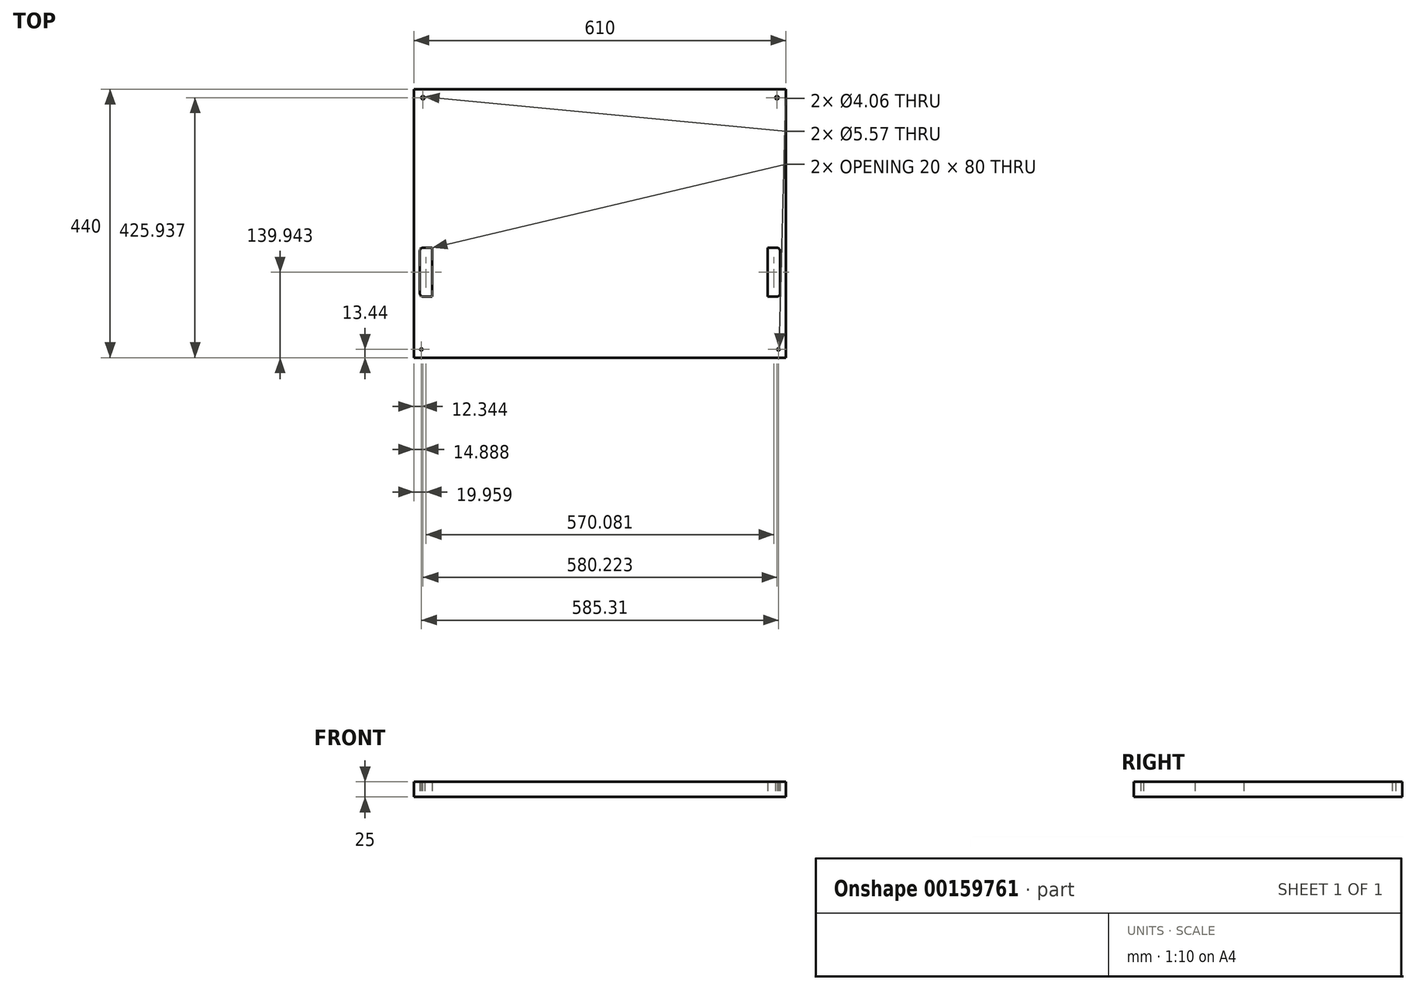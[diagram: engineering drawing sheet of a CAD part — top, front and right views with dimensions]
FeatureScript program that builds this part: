
annotation { "Feature Type Name" : "Feature", "Feature Type Description" : "" }
export const myFeature = defineFeature(function(context is Context, id is Id, definition is map)
    precondition{}
    {
        {
            var Q0;
            Q0=qCreatedBy(makeId("Top.planeOp"),FACE);
            var sketch = newSketch(context, id + "F0", { "sketchPlane" : qUnion([Q0])});
            skLineSegment(sketch, "E0.bottom", {"start": v(-71.6, 398.59) * mm, "end": v(538.4, 398.59) * mm});
            skLineSegment(sketch, "E0.top", {"start": v(-71.6, -41.41) * mm, "end": v(538.4, -41.41) * mm});
            skLineSegment(sketch, "E0.left", {"start": v(-71.6, 398.59) * mm, "end": v(-71.6, -41.41) * mm});
            skLineSegment(sketch, "E0.right", {"start": v(538.4, 398.59) * mm, "end": v(538.4, -41.41) * mm});
            skLineSegment(sketch, "E1", {"start": v(-61.63, 63.53) * mm, "end": v(-61.63, 133.53) * mm});
            skLineSegment(sketch, "E2", {"start": v(-56.63, 58.53) * mm, "end": v(-41.63, 58.53) * mm});
            skLineSegment(sketch, "E3", {"start": v(-41.63, 58.53) * mm, "end": v(-41.63, 138.53) * mm});
            skLineSegment(sketch, "E4", {"start": v(-41.63, 138.53) * mm, "end": v(-56.63, 138.53) * mm});
            skPoint(sketch, "E5.visualSharp", {"position": v(-61.63, 138.53) * mm});
            skArc(sketch, "E5.filletArc", {"start": v(-56.63, 138.53) * mm, "mid": v(-60.17, 137.07) * mm, "end": v(-61.63, 133.53) * mm});
            skPoint(sketch, "E6.visualSharp", {"position": v(-61.63, 58.53) * mm});
            skArc(sketch, "E6.filletArc", {"start": v(-61.63, 63.53) * mm, "mid": v(-60.17, 60) * mm, "end": v(-56.63, 58.53) * mm});
            skArc(sketch, "E7.MirrorCS", {"start": v(523.45, 138.53) * mm, "mid": v(526.98, 137.07) * mm, "end": v(528.45, 133.53) * mm});
            skArc(sketch, "E8.MirrorCS", {"start": v(528.45, 63.53) * mm, "mid": v(526.98, 60) * mm, "end": v(523.45, 58.53) * mm});
            skPoint(sketch, "E9.MirrorP", {"position": v(528.45, 138.53) * mm});
            skPoint(sketch, "E10.MirrorP", {"position": v(528.45, 58.53) * mm});
            skLineSegment(sketch, "E11.MirrorCS", {"start": v(523.45, 58.53) * mm, "end": v(508.45, 58.53) * mm});
            skLineSegment(sketch, "E12.MirrorCS", {"start": v(508.45, 138.53) * mm, "end": v(523.45, 138.53) * mm});
            skLineSegment(sketch, "E13.MirrorCS", {"start": v(508.45, 58.53) * mm, "end": v(508.45, 138.53) * mm});
            skLineSegment(sketch, "E14.MirrorCS", {"start": v(528.45, 63.53) * mm, "end": v(528.45, 133.53) * mm});
            skLineSegment(sketch, "E15", {"start": v(-38.6, 191.3) * mm, "end": v(-38.6, -53.17) * mm});
            skLineSegment(sketch, "E16", {"start": v(-38.6, 191.3) * mm, "end": v(-38.6, 443.73) * mm});
            skLineSegment(sketch, "E17.MirrorCS", {"start": v(505.4, 191.3) * mm, "end": v(505.4, -53.17) * mm});
            skLineSegment(sketch, "E18.MirrorCS", {"start": v(505.4, 191.3) * mm, "end": v(505.4, 443.73) * mm});
            skText(sketch, "E19", { "text": "v 90°", "fontName": "OpenSans-Regular.ttf"});
            skText(sketch, "E20", { "text": "v 90°", "fontName": "OpenSans-Regular.ttf"});
            skCircle(sketch, "E21", {"center": v(-56.7, 384.53) * mm, "radius": 2.79 * mm});
            skCircle(sketch, "E22", {"center": v(-59.25, -27.97) * mm, "radius": 2.03 * mm});
            skCircle(sketch, "E23.MirrorC", {"center": v(523.52, 384.53) * mm, "radius": 2.79 * mm});
            skCircle(sketch, "E24.MirrorC", {"center": v(526.06, -27.97) * mm, "radius": 2.03 * mm});
            const initialGuessF0  = {"E19": [-0.06044, 0.47023, 1, 0, 0.01693], "E20": [0.44904, 0.45417, 1, 0, 0.03012]};
            skSetInitialGuess(sketch, initialGuessF0);
            skSolve(sketch);
        }
        {
            var Q0;
            {var subQ0=sQuery(id+"F0.wireOp",EDGE,"E0.left");Q0=makeQuery(id+"F0.imprint","IMPRINT",FACE,{"disambiguationData":[TD([[makeQuery(id+"F0.imprint","IMPRINT",EDGE,{"derivedFrom":subQ0}),1.0]])]});}
            var Q1;
            {var subQ0=sQuery(id+"F0.wireOp",EDGE,"E16");var subQ3=sQuery(id+"F0.wireOp",EDGE,"E0.bottom");var subQ4=makeQuery(id+"F0.imprint","INTERSECT",VERTEX,{"derivedFrom":[subQ3,subQ0]});Q1=makeQuery(id+"F0.imprint","IMPRINT",FACE,{"disambiguationData":[TD([[makeQuery(id+"F0.imprint","IMPRINT",EDGE,{"disambiguationData":[TD([[subQ4,-1.0]])],"derivedFrom":subQ3}),-1.0]])]});}
            var Q2;
            {var subQ5=sQuery(id+"F0.wireOp",EDGE,"E0.right");Q2=makeQuery(id+"F0.imprint","IMPRINT",FACE,{"disambiguationData":[TD([[makeQuery(id+"F0.imprint","IMPRINT",EDGE,{"derivedFrom":subQ5}),-1.0]])]});}
            extrude(context, id + "F1", {"entities" : qUnion([Q0, Q1, Q2]), "depth" : 25 * mm});
        }
    });
